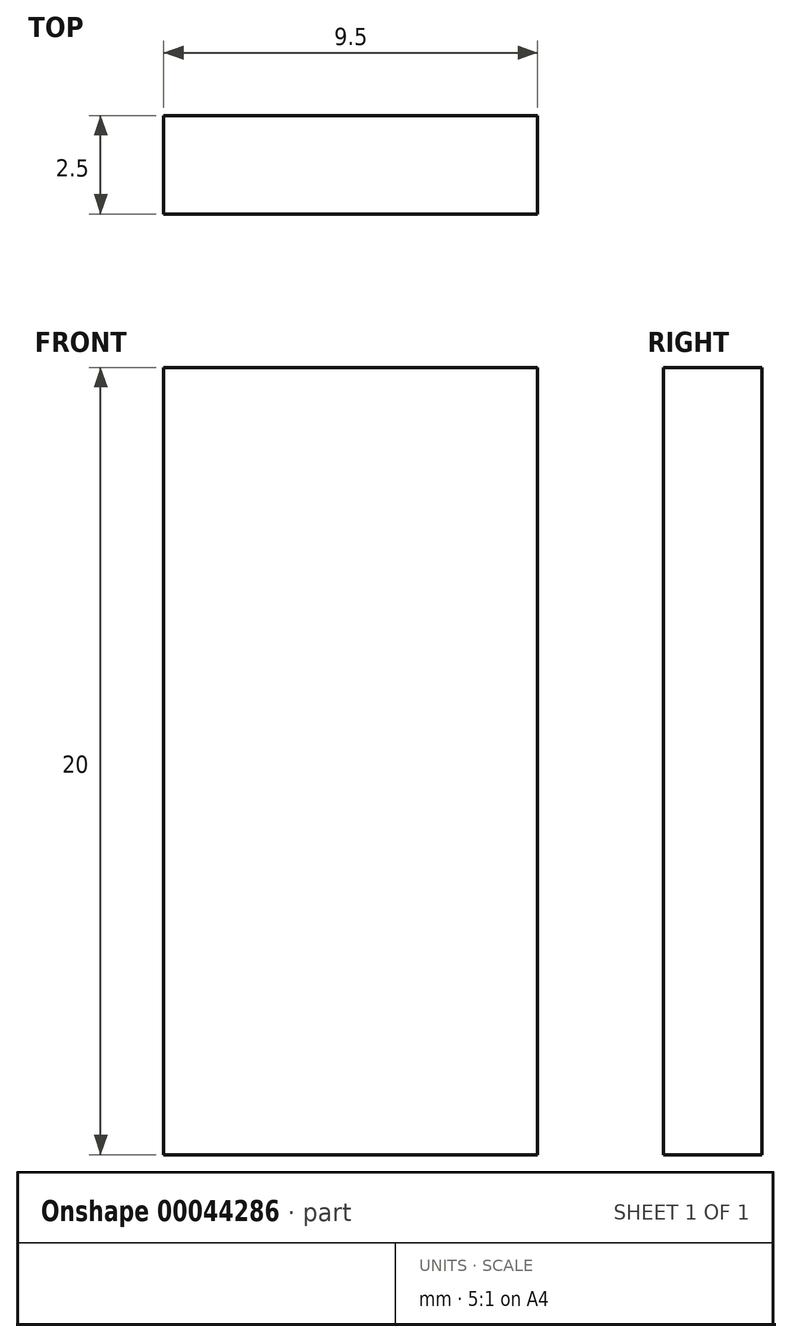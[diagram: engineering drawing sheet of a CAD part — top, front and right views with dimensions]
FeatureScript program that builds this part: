
annotation { "Feature Type Name" : "Feature", "Feature Type Description" : "" }
export const myFeature = defineFeature(function(context is Context, id is Id, definition is map)
    precondition{}
    {
        {
            var Q0;
            Q0=qCreatedBy(makeId("Front.planeOp"),FACE);
            var sketch = newSketch(context, id + "F0", { "sketchPlane" : qUnion([Q0])});
            skLineSegment(sketch, "E0.rect.bottom", {"start": v(-4.75, -10) * mm, "end": v(4.75, -10) * mm});
            skLineSegment(sketch, "E0.rect.top", {"start": v(-4.75, 10) * mm, "end": v(4.75, 10) * mm});
            skLineSegment(sketch, "E0.rect.left", {"start": v(-4.75, -10) * mm, "end": v(-4.75, 10) * mm});
            skLineSegment(sketch, "E0.rect.right", {"start": v(4.75, -10) * mm, "end": v(4.75, 10) * mm});
            skPoint(sketch, "E0.rect.middle", {"position": v(0, 0) * mm});
            skSolve(sketch);
        }
        {
            var Q0;
            Q0 = qSketchRegion(id + "F0", true);
            extrude(context, id + "F1", {"entities" : qUnion([Q0]), "oppositeDirection" : true, "depth" : 2.5 * mm});
        }
    });
